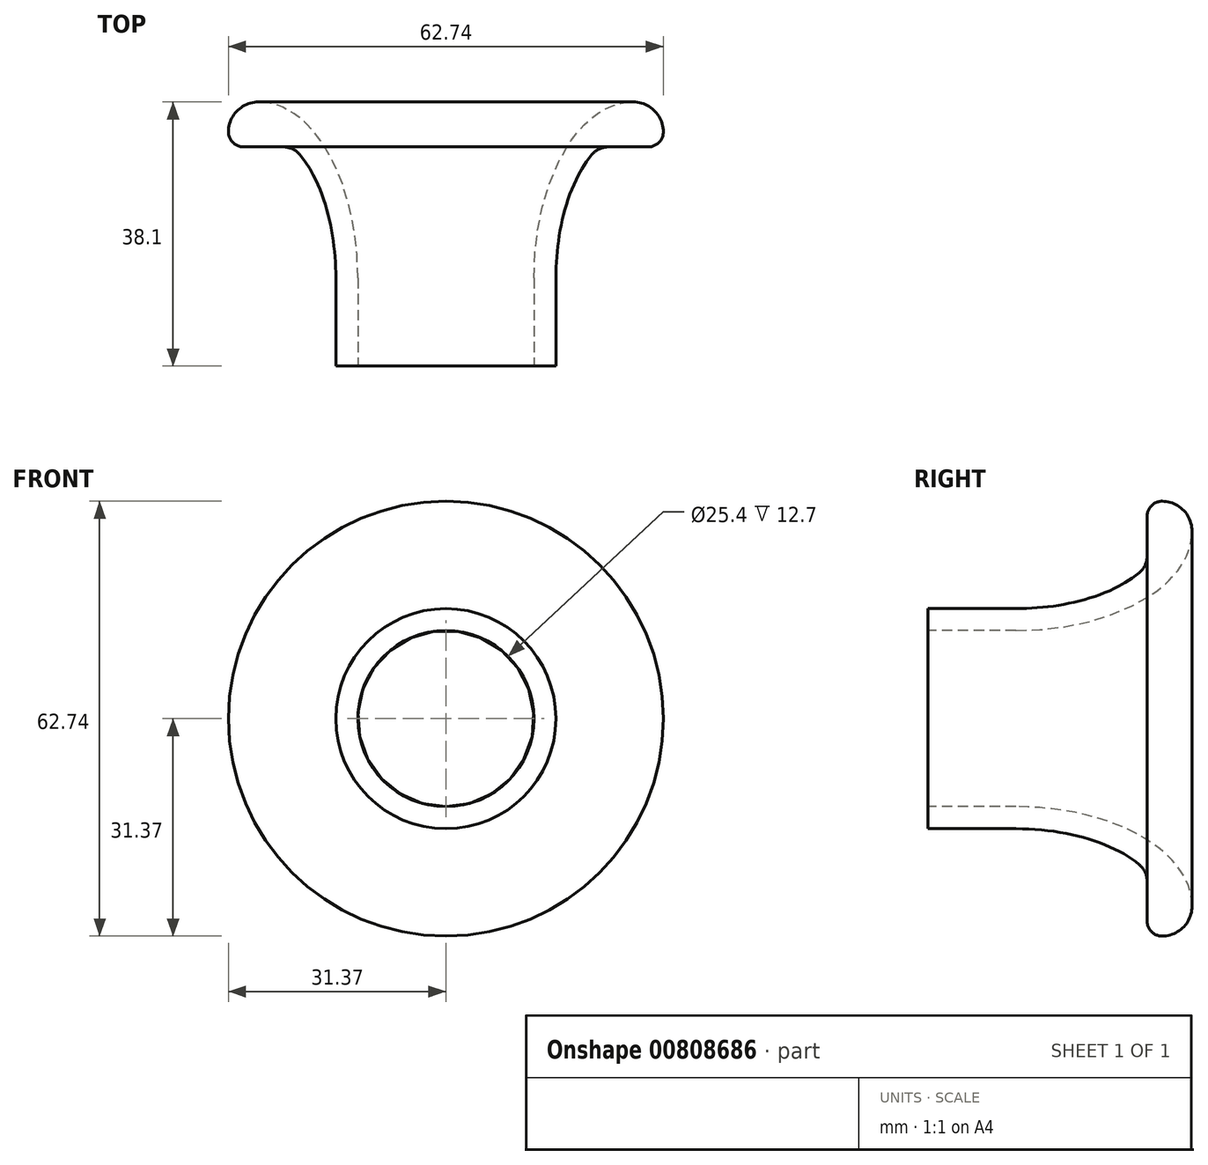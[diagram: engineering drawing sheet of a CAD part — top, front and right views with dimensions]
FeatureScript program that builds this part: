
annotation { "Feature Type Name" : "Feature", "Feature Type Description" : "" }
export const myFeature = defineFeature(function(context is Context, id is Id, definition is map)
    precondition{}
    {
        {
            var Q0;
            Q0=qCreatedBy(makeId("Top.planeOp"),FACE);
            var sketch = newSketch(context, id + "F0", { "sketchPlane" : qUnion([Q0])});
            skLineSegment(sketch, "E0", {"start": v(0, 0) * mm, "end": v(0, 70.34) * mm, "construction": true});
            skArc(sketch, "E1", {"start": v(31.37, 21.08) * mm, "mid": v(30.1, 24.14) * mm, "end": v(27.05, 25.4) * mm});
            skEllipticalArc(sketch, "E2", {});
            skLineSegment(sketch, "E3", {"start": v(15.88, 0) * mm, "end": v(15.88, -12.7) * mm});
            skLineSegment(sketch, "E4", {"start": v(15.88, -12.7) * mm, "end": v(12.7, -12.7) * mm});
            skLineSegment(sketch, "E5", {"start": v(12.7, -12.7) * mm, "end": v(12.7, 0) * mm});
            skEllipticalArc(sketch, "E6", {});
            skArc(sketch, "E7", {"start": v(29.21, 18.92) * mm, "mid": v(30.74, 19.56) * mm, "end": v(31.37, 21.08) * mm});
            skLineSegment(sketch, "E8", {"start": v(29.21, 18.92) * mm, "end": v(23.49, 18.92) * mm});
            skArc(sketch, "E9.filletArc", {"start": v(23.49, 18.92) * mm, "mid": v(22.14, 18.62) * mm, "end": v(21.04, 17.78) * mm});
            skLineSegment(sketch, "E10", {"start": v(0, 0) * mm, "end": v(12.7, 0) * mm, "construction": true});
            const initialGuessF0  = {"E2": [0.027051, 0, 0, 1, 0.0254, 0.014351, 0, 1.5707963267948966], "E6": [0.027051, 0, 0, 1, 0.021082, 0.011176, 0.5674091227015502, 1.5707963267948966]};
            skSetInitialGuess(sketch, initialGuessF0);
            skSolve(sketch);
        }
        {
            var Q0;
            Q0 = qSketchRegion(id + "F0", true);
            var Q1;
            Q1=sQuery(id+"F0.wireOp",EDGE,"E0");
            revolve(context, id + "F1", {"surfaceOperationType" : NewSurfaceOperationType.NEW, "entities" : qUnion([Q0]), "axis" : qUnion([Q1]), "revolveType" : RevolveType.FULL});
        }
    });
